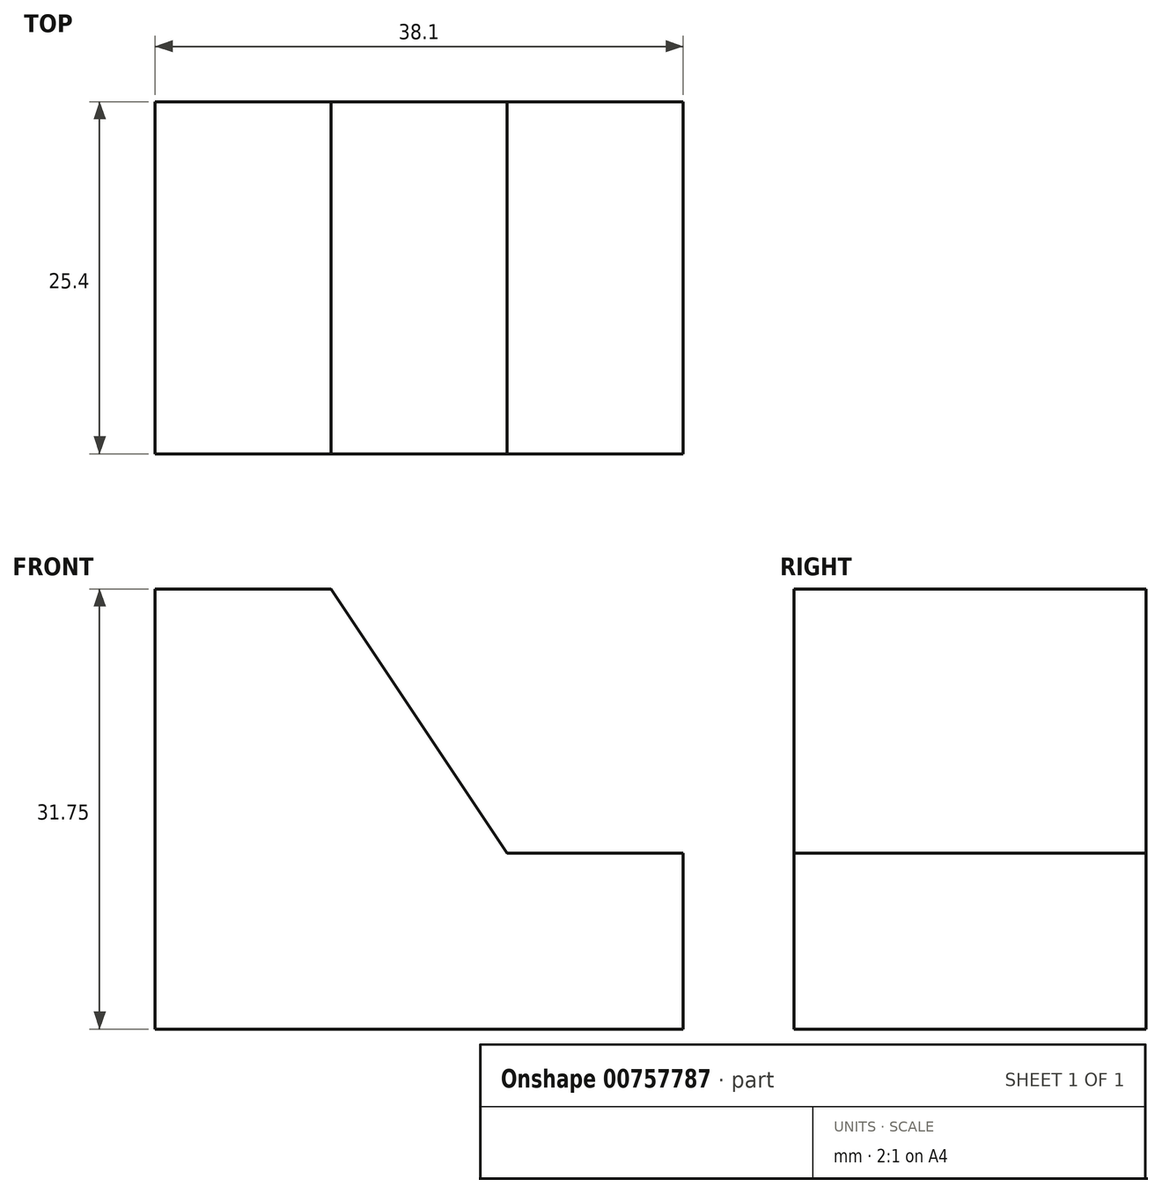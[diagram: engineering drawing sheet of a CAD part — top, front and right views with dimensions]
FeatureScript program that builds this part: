
annotation { "Feature Type Name" : "Feature", "Feature Type Description" : "" }
export const myFeature = defineFeature(function(context is Context, id is Id, definition is map)
    precondition{}
    {
        {
            var Q0;
            Q0=qCreatedBy(makeId("Front.planeOp"),FACE);
            var sketch = newSketch(context, id + "F0", { "sketchPlane" : qUnion([Q0])});
            skLineSegment(sketch, "E0", {"start": v(-20.85, 0) * mm, "end": v(17.25, 0) * mm});
            skLineSegment(sketch, "E1", {"start": v(17.25, 0) * mm, "end": v(17.25, 31.75) * mm});
            skLineSegment(sketch, "E2", {"start": v(17.25, 31.75) * mm, "end": v(-20.85, 31.75) * mm});
            skLineSegment(sketch, "E3", {"start": v(-20.85, 31.75) * mm, "end": v(-20.85, 0) * mm});
            skSolve(sketch);
        }
        {
            var Q0;
            Q0 = qSketchRegion(id + "F0", true);
            extrude(context, id + "F1", {"entities" : qUnion([Q0]), "depth" : 25.4 * mm, "offsetDistance" : 25.4 * mm});
        }
        {
            var Q0;
            Q0=makeQuery(id+"F1.opExtrude","CAP_FACE",FACE,{"disambiguationData":[OSD([sQuery(id+"F0.wireOp",EDGE,"E0"),sQuery(id+"F0.wireOp",EDGE,"E1"),sQuery(id+"F0.wireOp",EDGE,"E2"),sQuery(id+"F0.wireOp",EDGE,"E3")])],"isStart":false});
            var sketch = newSketch(context, id + "F2", { "sketchPlane" : qUnion([Q0])});
            skLineSegment(sketch, "E4", {"start": v(17.25, 12.7) * mm, "end": v(4.55, 12.7) * mm});
            skLineSegment(sketch, "E5", {"start": v(4.55, 12.7) * mm, "end": v(-8.15, 31.75) * mm});
            skSolve(sketch);
        }
        {
            var Q0;
            Q0 = qSketchRegion(id + "F2", true);
            var Q1;
            {var subQ0=sQuery(id+"F2.wireOp",EDGE,"E4");Q1=makeQuery(id+"F2.imprint","IMPRINT",FACE,{"disambiguationData":[TD([[makeQuery(id+"F2.imprint","IMPRINT",EDGE,{"derivedFrom":subQ0}),-1.0]])]});}
            extrude(context, id + "F3", {"entities" : qUnion([Q0, Q1]), "operationType" : NewBodyOperationType.REMOVE, "endBound" : BoundingType.THROUGH_ALL, "oppositeDirection" : true, "depth" : 25.4 * mm, "offsetDistance" : 25.4 * mm});
        }
    });
